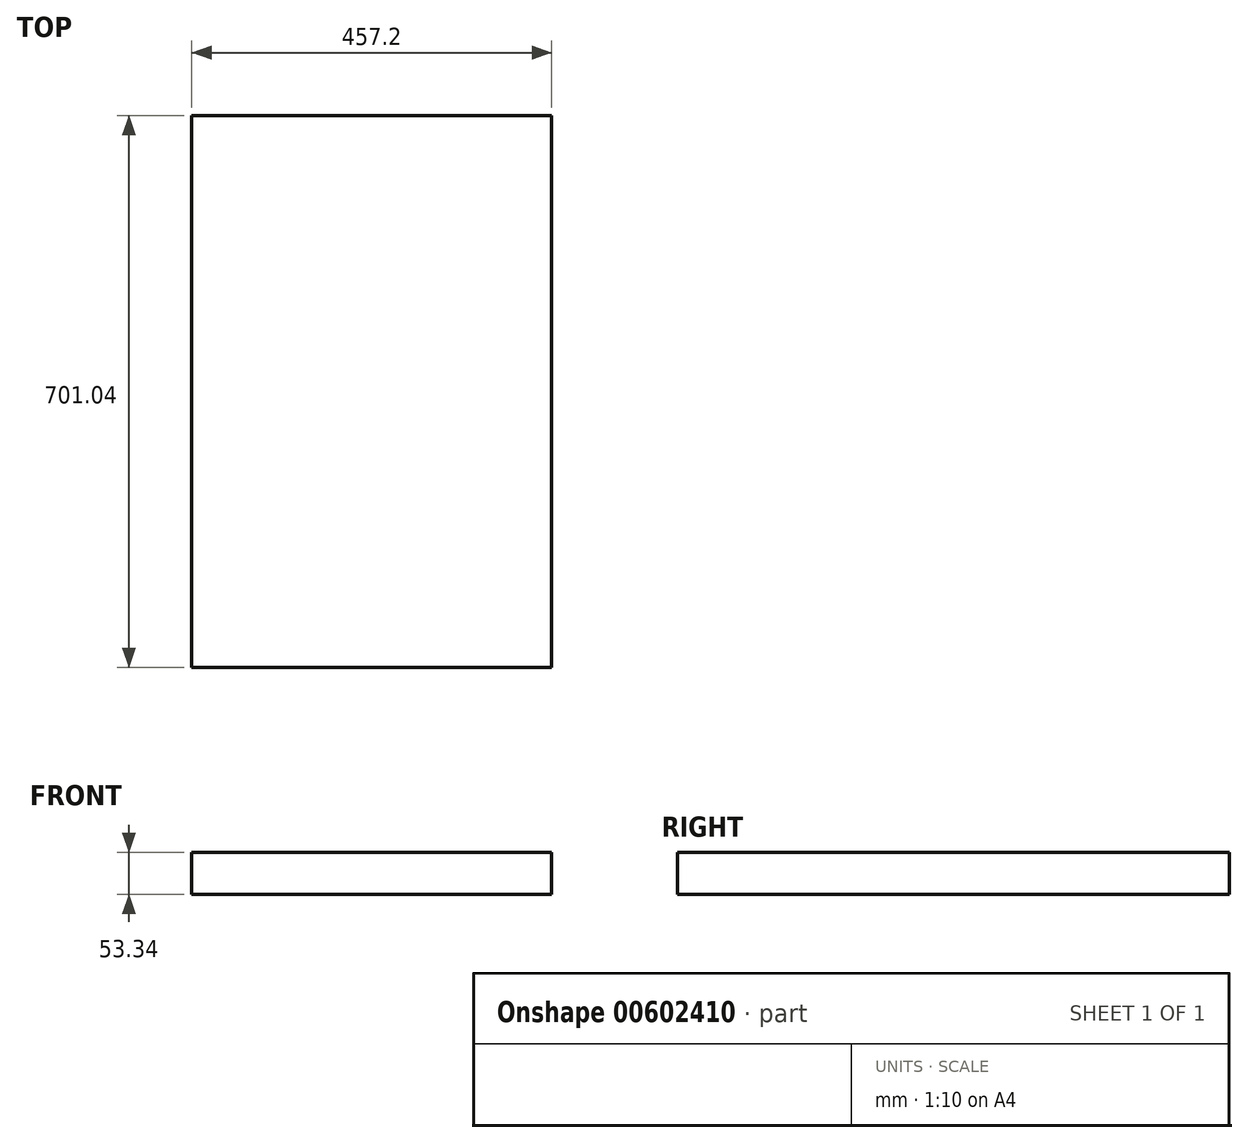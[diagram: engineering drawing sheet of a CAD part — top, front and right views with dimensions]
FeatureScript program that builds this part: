
annotation { "Feature Type Name" : "Feature", "Feature Type Description" : "" }
export const myFeature = defineFeature(function(context is Context, id is Id, definition is map)
    precondition{}
    {
        {
            var Q0;
            Q0=qCreatedBy(makeId("Top.planeOp"),FACE);
            var sketch = newSketch(context, id + "F0", { "sketchPlane" : qUnion([Q0])});
            skLineSegment(sketch, "E0.bottom", {"start": v(0, 0) * mm, "end": v(457.2, 0) * mm});
            skLineSegment(sketch, "E0.top", {"start": v(0, -701.04) * mm, "end": v(457.2, -701.04) * mm});
            skLineSegment(sketch, "E0.left", {"start": v(0, 0) * mm, "end": v(0, -701.04) * mm});
            skLineSegment(sketch, "E0.right", {"start": v(457.2, 0) * mm, "end": v(457.2, -701.04) * mm});
            skSolve(sketch);
        }
        {
            var Q0;
            Q0=makeQuery(id+"F0.imprint","IMPRINT",FACE,{"disambiguationData":[TD([[makeQuery(id+"F0.imprint","IMPRINT",EDGE,{"derivedFrom":sQuery(id+"F0.wireOp",EDGE,"E0.bottom")}),-1.0]])]});
            extrude(context, id + "F1", {"entities" : qUnion([Q0]), "depth" : 53.34 * mm, "offsetDistance" : 30.48 * mm});
        }
    });
